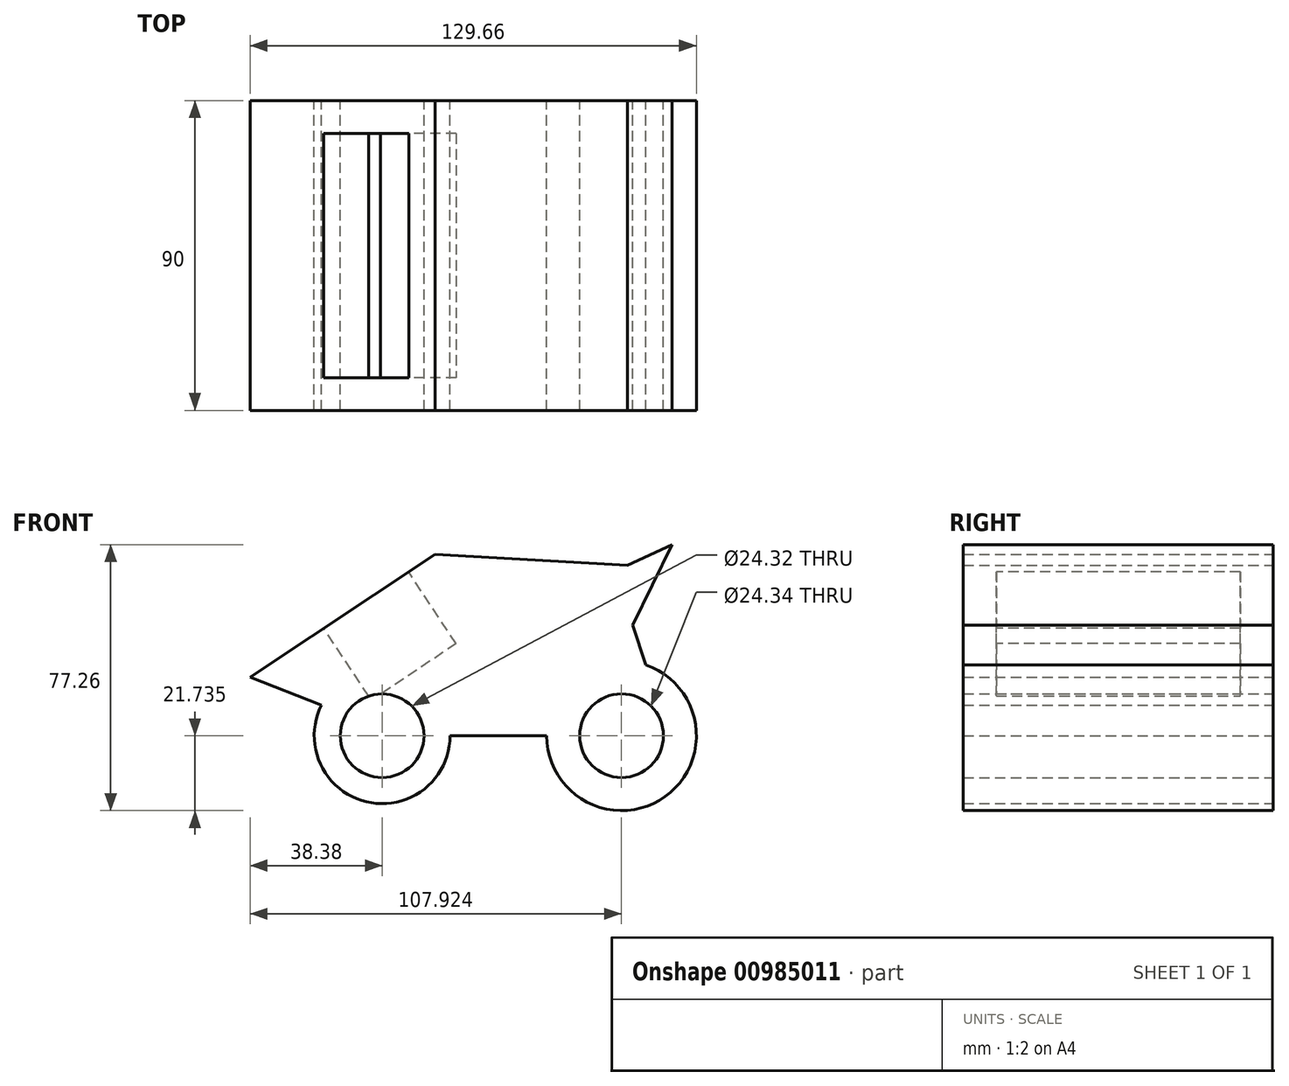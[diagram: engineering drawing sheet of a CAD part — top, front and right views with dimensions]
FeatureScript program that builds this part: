
annotation { "Feature Type Name" : "Feature", "Feature Type Description" : "" }
export const myFeature = defineFeature(function(context is Context, id is Id, definition is map)
    precondition{}
    {
        {
            var Q0;
            Q0=qCreatedBy(makeId("Front.planeOp"),FACE);
            var sketch = newSketch(context, id + "F0", { "sketchPlane" : qUnion([Q0])});
            skCircle(sketch, "E0", {"center": v(0, -2.12) * mm, "radius": 12.16 * mm});
            skLineSegment(sketch, "E1", {"start": v(0, -2.12) * mm, "end": v(69.54, -2.12) * mm});
            skCircle(sketch, "E2", {"center": v(69.54, -2.12) * mm, "radius": 12.17 * mm});
            skLineSegment(sketch, "E3", {"start": v(0, 0) * mm, "end": v(-38.38, 14.87) * mm});
            skLineSegment(sketch, "E4", {"start": v(-38.38, 14.87) * mm, "end": v(15.44, 50.56) * mm});
            skLineSegment(sketch, "E5", {"start": v(15.44, 50.56) * mm, "end": v(71.24, 47.45) * mm});
            skLineSegment(sketch, "E6", {"start": v(71.24, 47.45) * mm, "end": v(84.27, 53.4) * mm});
            skLineSegment(sketch, "E7", {"start": v(84.27, 53.4) * mm, "end": v(72.74, 29.96) * mm});
            skLineSegment(sketch, "E8", {"start": v(72.74, 29.96) * mm, "end": v(76.98, 17.13) * mm});
            skLineSegment(sketch, "E9", {"start": v(76.98, 17.13) * mm, "end": v(69.54, -2.12) * mm});
            skCircle(sketch, "E10", {"center": v(0, -2.12) * mm, "radius": 19.74 * mm});
            skCircle(sketch, "E11", {"center": v(69.54, -2.12) * mm, "radius": 21.74 * mm});
            skSolve(sketch);
        }
        {
            var Q0;
            {var subQ0=sQuery(id+"F0.wireOp",EDGE,"E1");var subQ1=sQuery(id+"F0.wireOp",EDGE,"E0");var subQ2=makeQuery(id+"F0.imprint","INTERSECT",VERTEX,{"derivedFrom":[subQ1,subQ0]});Q0=makeQuery(id+"F0.imprint","IMPRINT",FACE,{"disambiguationData":[TD([[makeQuery(id+"F0.imprint","IMPRINT",EDGE,{"disambiguationData":[TD([[subQ2,1.0]])],"derivedFrom":subQ1}),-1.0]])]});}
            var Q1;
            {var subQ0=sQuery(id+"F0.wireOp",EDGE,"E4");Q1=makeQuery(id+"F0.imprint","IMPRINT",FACE,{"disambiguationData":[TD([[makeQuery(id+"F0.imprint","IMPRINT",EDGE,{"derivedFrom":subQ0}),-1.0]])]});}
            var Q2;
            {var subQ5=sQuery(id+"F0.wireOp",EDGE,"E11");var subQ7=sQuery(id+"F0.wireOp",EDGE,"E1");var subQ8=makeQuery(id+"F0.imprint","INTERSECT",VERTEX,{"derivedFrom":[subQ7,subQ5]});Q2=makeQuery(id+"F0.imprint","IMPRINT",FACE,{"disambiguationData":[TD([[makeQuery(id+"F0.imprint","IMPRINT",EDGE,{"disambiguationData":[TD([[subQ8,-1.0]])],"derivedFrom":subQ7}),-1.0]])]});}
            var Q3;
            {var subQ0=sQuery(id+"F0.wireOp",EDGE,"E1");var subQ1=sQuery(id+"F0.wireOp",EDGE,"E0");var subQ2=makeQuery(id+"F0.imprint","INTERSECT",VERTEX,{"derivedFrom":[subQ1,subQ0]});Q3=makeQuery(id+"F0.imprint","IMPRINT",FACE,{"disambiguationData":[TD([[makeQuery(id+"F0.imprint","IMPRINT",EDGE,{"disambiguationData":[TD([[subQ2,-1.0]])],"derivedFrom":subQ1}),-1.0]])]});}
            var Q4;
            {var subQ3=sQuery(id+"F0.wireOp",EDGE,"E11");var subQ5=sQuery(id+"F0.wireOp",EDGE,"E1");var subQ6=makeQuery(id+"F0.imprint","INTERSECT",VERTEX,{"derivedFrom":[subQ5,subQ3]});Q4=makeQuery(id+"F0.imprint","IMPRINT",FACE,{"disambiguationData":[TD([[makeQuery(id+"F0.imprint","IMPRINT",EDGE,{"disambiguationData":[TD([[subQ6,-1.0]])],"derivedFrom":subQ5}),1.0]])]});}
            extrude(context, id + "F1", {"entities" : qUnion([Q0, Q1, Q2, Q3, Q4]), "depth" : 90 * mm, "offsetDistance" : 25 * mm});
        }
        {
            var Q0;
            Q0=makeQuery(id+"F1.opExtrude","SWEPT_FACE",FACE,{"disambiguationData":[OSD([sQuery(id+"F0.wireOp",EDGE,"E4")])]});
            var sketch = newSketch(context, id + "F2", { "sketchPlane" : qUnion([Q0])});
            skLineSegment(sketch, "E12", {"start": v(40.81, -45) * mm, "end": v(-23.77, -45) * mm, "construction": true});
            skLineSegment(sketch, "E13.bottom", {"start": v(31.56, -9.55) * mm, "end": v(1.91, -9.55) * mm});
            skLineSegment(sketch, "E13.top", {"start": v(31.56, -80.45) * mm, "end": v(1.91, -80.45) * mm});
            skLineSegment(sketch, "E13.left", {"start": v(31.56, -9.55) * mm, "end": v(31.56, -80.45) * mm});
            skLineSegment(sketch, "E13.right", {"start": v(1.91, -9.55) * mm, "end": v(1.91, -80.45) * mm});
            skPoint(sketch, "E13.middle", {"position": v(16.73, -45) * mm});
            skSolve(sketch);
        }
        {
            var Q0;
            Q0=makeQuery(id+"F2.imprint","IMPRINT",FACE,{"disambiguationData":[TD([[makeQuery(id+"F2.imprint","IMPRINT",EDGE,{"derivedFrom":sQuery(id+"F2.wireOp",EDGE,"E13.bottom")}),1.0]])]});
            extrude(context, id + "F3", {"entities" : qUnion([Q0]), "operationType" : NewBodyOperationType.REMOVE, "oppositeDirection" : true, "depth" : 25 * mm, "offsetDistance" : 25 * mm});
        }
    });
